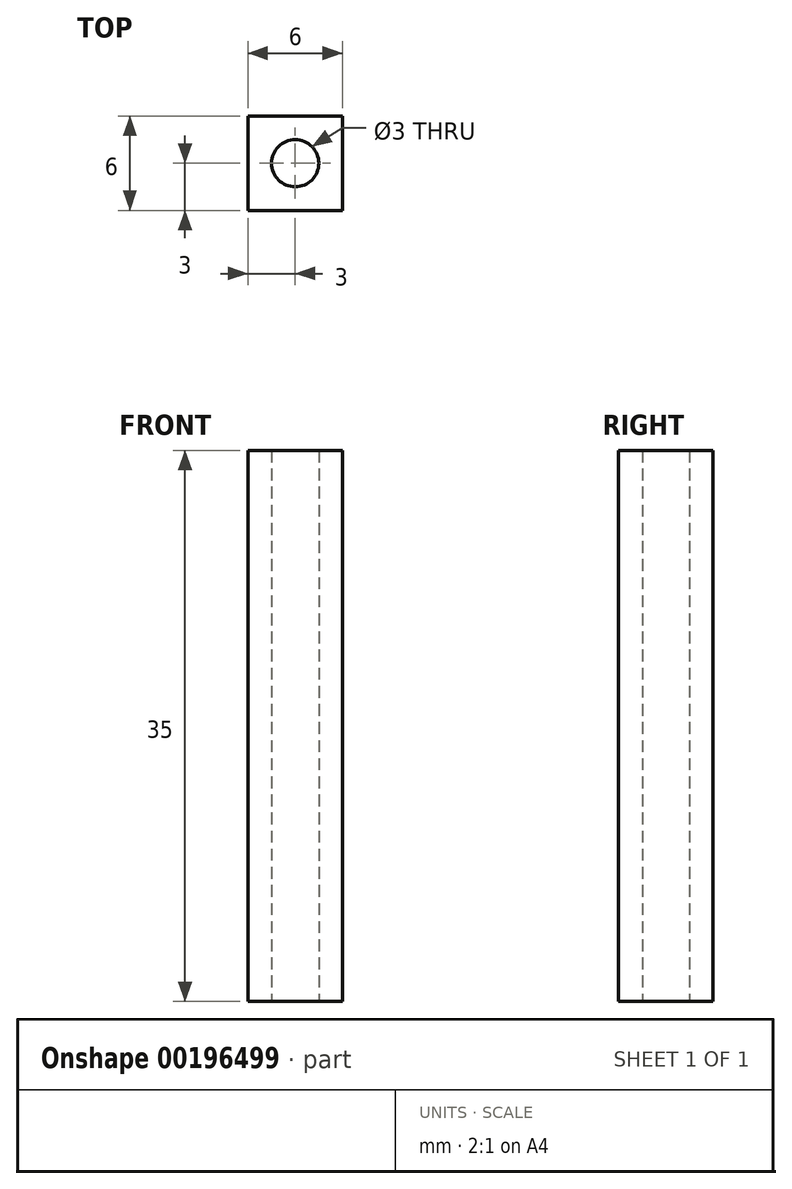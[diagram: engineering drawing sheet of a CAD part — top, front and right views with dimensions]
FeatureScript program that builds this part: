
annotation { "Feature Type Name" : "Feature", "Feature Type Description" : "" }
export const myFeature = defineFeature(function(context is Context, id is Id, definition is map)
    precondition{}
    {
        {
            assignVariable(context, id + "F0", {"name" : "h", "anyValue" : 35});
        }
        {
            var Q0;
            Q0=qCreatedBy(makeId("Top.planeOp"),FACE);
            var sketch = newSketch(context, id + "F1", { "sketchPlane" : qUnion([Q0])});
            skCircle(sketch, "E0", {"center": v(0, 0) * mm, "radius": 1.5 * mm});
            skLineSegment(sketch, "E1.bottom", {"start": v(3, -3) * mm, "end": v(-3, -3) * mm});
            skLineSegment(sketch, "E1.top", {"start": v(3, 3) * mm, "end": v(-3, 3) * mm});
            skLineSegment(sketch, "E1.left", {"start": v(3, -3) * mm, "end": v(3, 3) * mm});
            skLineSegment(sketch, "E1.right", {"start": v(-3, -3) * mm, "end": v(-3, 3) * mm});
            skSolve(sketch);
        }
        {
            var Q0;
            Q0=makeQuery(id+"F1.imprint","IMPRINT",FACE,{"disambiguationData":[TD([[makeQuery(id+"F1.imprint","IMPRINT",EDGE,{"derivedFrom":sQuery(id+"F1.wireOp",EDGE,"E0")}),-1.0]])]});
            extrude(context, id + "F2", {"entities" : qUnion([Q0]), "depth" : (getVariable(context, 'h')) * mm});
        }
    });
